# Revit family: 31_DoorOpening
name_source: partatom
category: Doors
units: mm (PartAtom-declared; Revit-internal decimal feet)

## family parameters
Always vertical = Yes
Cut with Voids When Loaded = No
Host = Wall
OmniClass Number = 23.30.10.00
OmniClass Title = Doors
Room Calculation Point = No
Shared = No

## types (7) — shared parameters
zero-valued in all types: Height, Width

## per-type parameters (varying)
| type | Function | Rough Height | Rough Width |
| 0915 x 2134mm | Interior | 2134 mm  [stored 7.00131 ft] | 915 mm  [stored 3.00197 ft] |
| 0762 x 2134mm | Interior | 2134 mm  [stored 7.00131 ft] | 762 mm  [stored 2.5 ft] |
| 0762 x 2032mm | Exterior | 2032 mm | 762 mm  [stored 2.5 ft] |
| 0813 x 2134mm | Interior | 2134 mm  [stored 7.00131 ft] | 813 mm |
| 0864 x 2032mm | Interior | 2032 mm | 864 mm  [stored 2.83465 ft] |
| 0864 x 2134mm | Interior | 2134 mm  [stored 7.00131 ft] | 864 mm  [stored 2.83465 ft] |
| 0915 x 2032mm | Interior | 2032 mm | 915 mm  [stored 3.00197 ft] |

note: [stored X ft] marks values corroborated as IEEE doubles in the binary element streams (Revit-internal decimal feet)

## geometry (parser evidence)
native form markers: Sweep x2
no freeform markers — native parametric forms only
